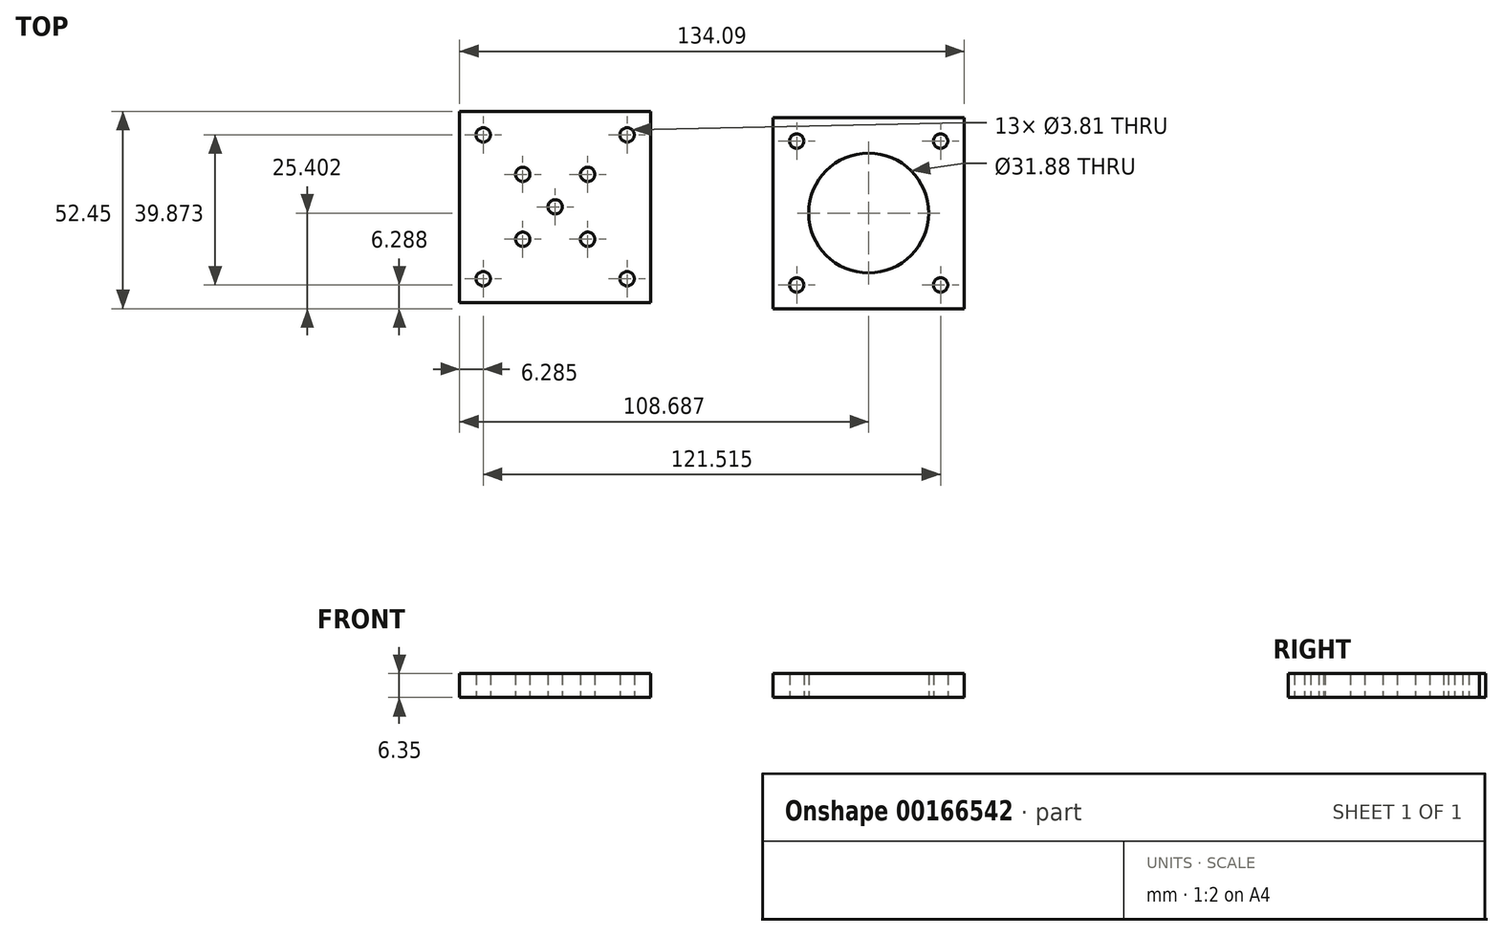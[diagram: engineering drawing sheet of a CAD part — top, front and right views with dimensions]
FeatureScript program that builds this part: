
annotation { "Feature Type Name" : "Feature", "Feature Type Description" : "" }
export const myFeature = defineFeature(function(context is Context, id is Id, definition is map)
    precondition{}
    {
        {
            var Q0;
            Q0=qCreatedBy(makeId("Top.planeOp"),FACE);
            var sketch = newSketch(context, id + "F0", { "sketchPlane" : qUnion([Q0])});
            skLineSegment(sketch, "E0.bottom", {"start": v(-69.13, 75.74) * mm, "end": v(-18.33, 75.74) * mm});
            skLineSegment(sketch, "E0.top", {"start": v(-69.13, 24.94) * mm, "end": v(-18.33, 24.94) * mm});
            skLineSegment(sketch, "E0.left", {"start": v(-69.13, 75.74) * mm, "end": v(-69.13, 24.94) * mm});
            skLineSegment(sketch, "E0.right", {"start": v(-18.33, 75.74) * mm, "end": v(-18.33, 24.94) * mm});
            skLineSegment(sketch, "E1", {"start": v(-69.13, 24.94) * mm, "end": v(-18.33, 75.74) * mm});
            skLineSegment(sketch, "E2", {"start": v(-18.33, 24.94) * mm, "end": v(-69.13, 75.74) * mm});
            skCircle(sketch, "E3", {"center": v(-43.73, 50.34) * mm, "radius": 1.9 * mm});
            skCircle(sketch, "E4", {"center": v(-62.84, 69.45) * mm, "radius": 1.9 * mm});
            skCircle(sketch, "E5", {"center": v(-62.84, 31.22) * mm, "radius": 1.9 * mm});
            skCircle(sketch, "E6", {"center": v(-24.62, 31.22) * mm, "radius": 1.9 * mm});
            skCircle(sketch, "E7", {"center": v(-24.62, 69.45) * mm, "radius": 1.9 * mm});
            skCircle(sketch, "E8", {"center": v(-52.35, 41.72) * mm, "radius": 1.9 * mm});
            skCircle(sketch, "E9", {"center": v(-35.1, 41.72) * mm, "radius": 1.9 * mm});
            skCircle(sketch, "E10", {"center": v(-35.1, 58.96) * mm, "radius": 1.9 * mm});
            skCircle(sketch, "E11", {"center": v(-52.35, 58.96) * mm, "radius": 1.9 * mm});
            skSolve(sketch);
        }
        {
            var Q0;
            Q0 = qSketchRegion(id + "F0", true);
            extrude(context, id + "F1", {"entities" : qUnion([Q0]), "depth" : 6.35 * mm});
        }
        {
            var Q0;
            Q0=qCreatedBy(makeId("Top.planeOp"),FACE);
            var sketch = newSketch(context, id + "F2", { "sketchPlane" : qUnion([Q0])});
            skLineSegment(sketch, "E12.bottom", {"start": v(14.16, 74.1) * mm, "end": v(64.96, 74.1) * mm});
            skLineSegment(sketch, "E12.top", {"start": v(14.16, 23.3) * mm, "end": v(64.96, 23.3) * mm});
            skLineSegment(sketch, "E12.left", {"start": v(14.16, 74.1) * mm, "end": v(14.16, 23.3) * mm});
            skLineSegment(sketch, "E12.right", {"start": v(64.96, 74.1) * mm, "end": v(64.96, 23.3) * mm});
            skLineSegment(sketch, "E13", {"start": v(14.16, 23.3) * mm, "end": v(64.96, 74.1) * mm});
            skLineSegment(sketch, "E14", {"start": v(64.96, 23.3) * mm, "end": v(14.16, 74.1) * mm});
            skCircle(sketch, "E15", {"center": v(39.56, 48.7) * mm, "radius": 15.94 * mm});
            skCircle(sketch, "E16", {"center": v(20.44, 29.58) * mm, "radius": 1.9 * mm});
            skCircle(sketch, "E17", {"center": v(58.67, 29.58) * mm, "radius": 1.9 * mm});
            skCircle(sketch, "E18", {"center": v(58.67, 67.8) * mm, "radius": 1.9 * mm});
            skCircle(sketch, "E19", {"center": v(20.44, 67.8) * mm, "radius": 1.9 * mm});
            skSolve(sketch);
        }
        {
            var Q0;
            Q0 = qSketchRegion(id + "F2", true);
            extrude(context, id + "F3", {"entities" : qUnion([Q0]), "depth" : 6.35 * mm});
        }
    });
